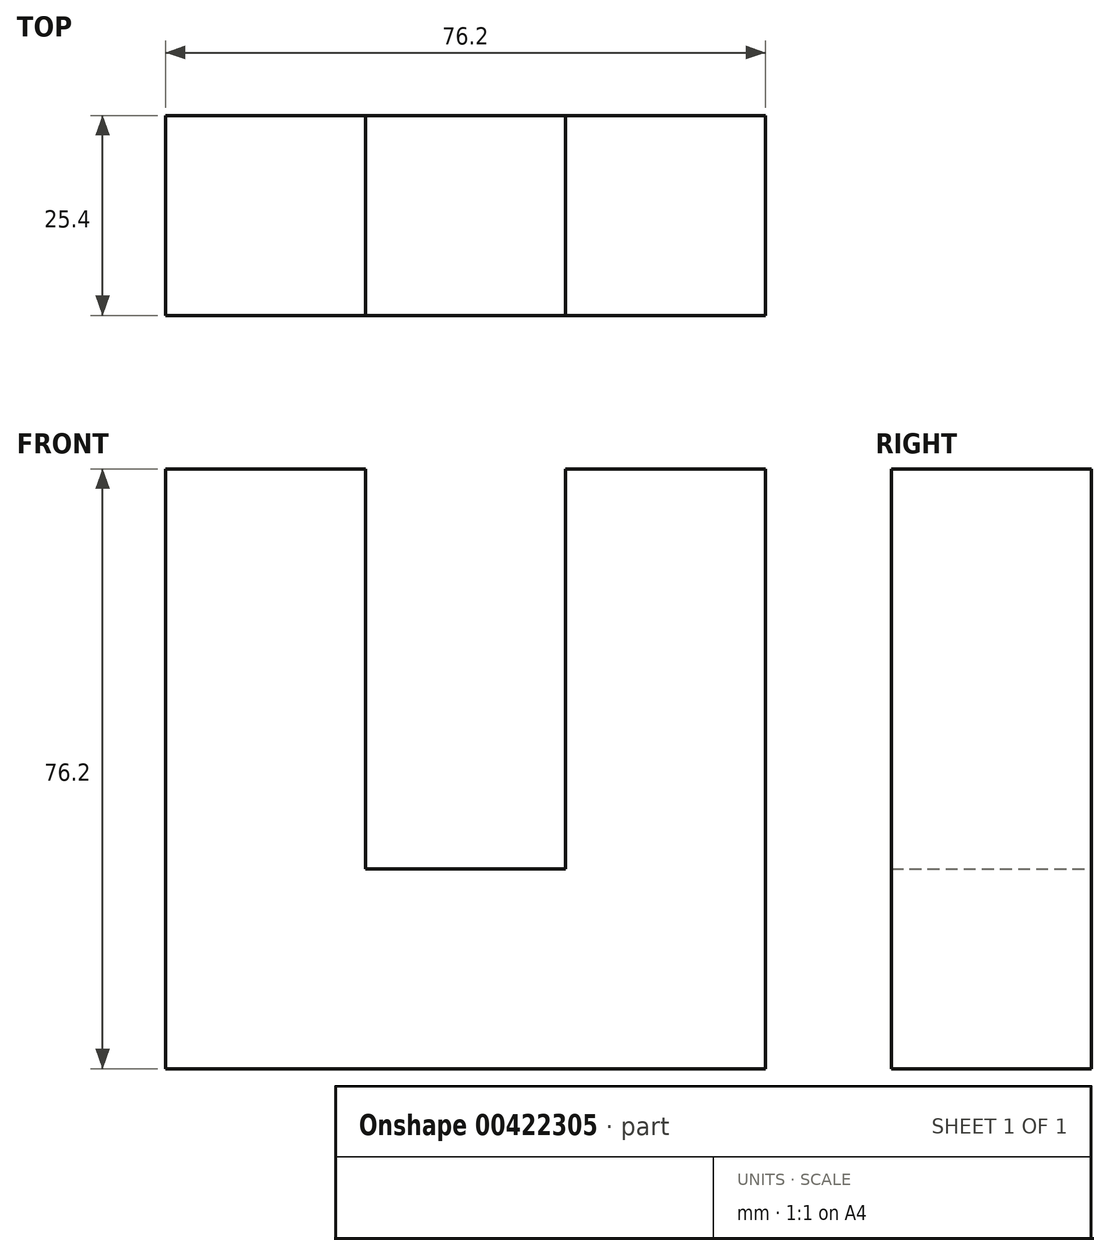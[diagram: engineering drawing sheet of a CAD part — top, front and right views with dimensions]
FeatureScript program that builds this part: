
annotation { "Feature Type Name" : "Feature", "Feature Type Description" : "" }
export const myFeature = defineFeature(function(context is Context, id is Id, definition is map)
    precondition{}
    {
        {
            var Q0;
            Q0=qCreatedBy(makeId("Front.planeOp"),FACE);
            var sketch = newSketch(context, id + "F0", { "sketchPlane" : qUnion([Q0])});
            skLineSegment(sketch, "E0", {"start": v(-45.4, -40.39) * mm, "end": v(30.8, -40.39) * mm});
            skLineSegment(sketch, "E1", {"start": v(-45.4, -40.39) * mm, "end": v(-45.4, 35.81) * mm});
            skLineSegment(sketch, "E2", {"start": v(-45.4, 35.81) * mm, "end": v(-20, 35.81) * mm});
            skLineSegment(sketch, "E3", {"start": v(-20, 35.81) * mm, "end": v(-20, -14.99) * mm});
            skLineSegment(sketch, "E4", {"start": v(-20, -14.99) * mm, "end": v(5.4, -14.99) * mm});
            skLineSegment(sketch, "E5", {"start": v(5.4, -14.99) * mm, "end": v(5.4, 35.81) * mm});
            skLineSegment(sketch, "E6", {"start": v(5.4, 35.81) * mm, "end": v(30.8, 35.81) * mm});
            skLineSegment(sketch, "E7", {"start": v(30.8, 35.81) * mm, "end": v(30.8, -40.39) * mm});
            skSolve(sketch);
        }
        {
            var Q0;
            Q0 = qSketchRegion(id + "F0", true);
            extrude(context, id + "F1", {"entities" : qUnion([Q0]), "depth" : 25.4 * mm});
        }
    });
